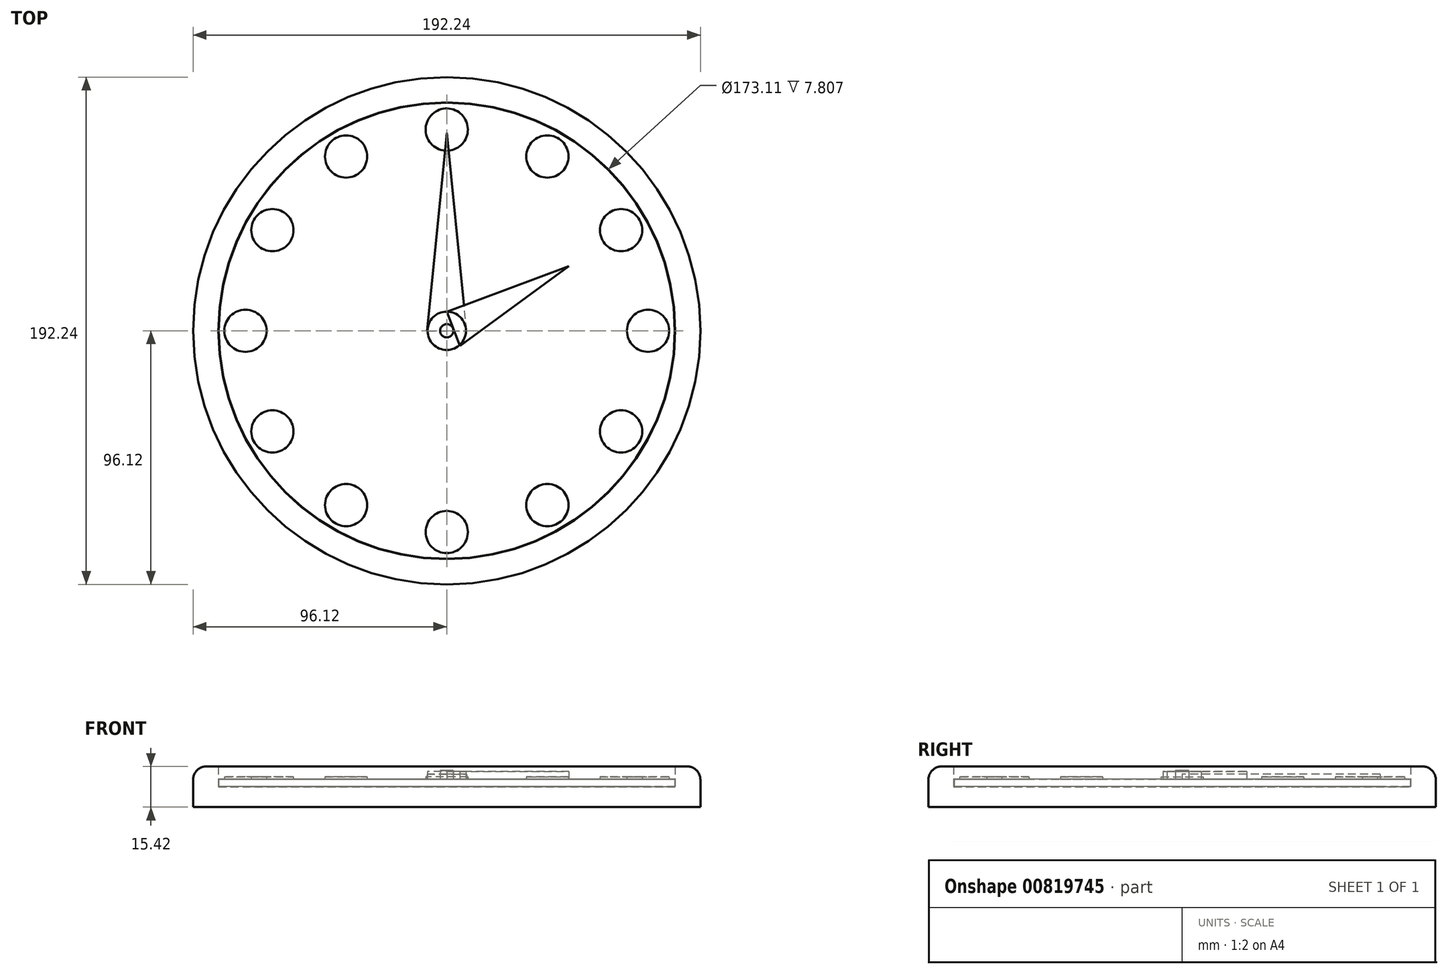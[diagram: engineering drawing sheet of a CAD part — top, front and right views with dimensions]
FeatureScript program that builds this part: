
annotation { "Feature Type Name" : "Feature", "Feature Type Description" : "" }
export const myFeature = defineFeature(function(context is Context, id is Id, definition is map)
    precondition{}
    {
        {
            var Q0;
            Q0=qCreatedBy(makeId("Front.planeOp"),FACE);
            var sketch = newSketch(context, id + "F0", { "sketchPlane" : qUnion([Q0])});
            skLineSegment(sketch, "E0", {"start": v(-96.12, 15.42) * mm, "end": v(-86.56, 15.42) * mm});
            skLineSegment(sketch, "E1", {"start": v(-86.56, 15.42) * mm, "end": v(-86.56, 7.61) * mm});
            skLineSegment(sketch, "E2", {"start": v(-86.56, 7.61) * mm, "end": v(0, 7.61) * mm});
            skLineSegment(sketch, "E3", {"start": v(0, 7.61) * mm, "end": v(0, 0) * mm});
            skLineSegment(sketch, "E4", {"start": v(0, 7.61) * mm, "end": v(0, 30.45) * mm, "construction": true});
            skLineSegment(sketch, "E5", {"start": v(-96.12, 15.42) * mm, "end": v(-96.12, 0) * mm});
            skLineSegment(sketch, "E6", {"start": v(-96.12, 0) * mm, "end": v(0, 0) * mm});
            skSolve(sketch);
        }
        {
            var Q0;
            Q0=makeQuery(id+"F0.imprint","IMPRINT",FACE,{"disambiguationData":[TD([[makeQuery(id+"F0.imprint","IMPRINT",EDGE,{"derivedFrom":sQuery(id+"F0.wireOp",EDGE,"E0")}),-1.0]])]});
            var Q1;
            Q1=sQuery(id+"F0.wireOp",EDGE,"E4");
            revolve(context, id + "F1", {"surfaceOperationType" : NewSurfaceOperationType.NEW, "entities" : qUnion([Q0]), "axis" : qUnion([Q1]), "revolveType" : RevolveType.FULL});
        }
        {
            var Q0;
            Q0=qCreatedBy(makeId("Right.planeOp"),FACE);
            var sketch = newSketch(context, id + "F2", { "sketchPlane" : qUnion([Q0])});
            skLineSegment(sketch, "E7", {"start": v(-86.42, 10.54) * mm, "end": v(0, 10.54) * mm});
            skLineSegment(sketch, "E8", {"start": v(0, 10.54) * mm, "end": v(0, 7.8) * mm});
            skLineSegment(sketch, "E9", {"start": v(0, 7.8) * mm, "end": v(-86.42, 7.8) * mm});
            skLineSegment(sketch, "E10", {"start": v(-86.42, 7.8) * mm, "end": v(-86.42, 10.54) * mm});
            skSolve(sketch);
        }
        {
            var Q0;
            Q0=makeQuery(id+"F2.imprint","IMPRINT",FACE,{"disambiguationData":[TD([[makeQuery(id+"F2.imprint","IMPRINT",EDGE,{"derivedFrom":sQuery(id+"F2.wireOp",EDGE,"E7")}),-1.0]])]});
            var Q1;
            Q1=sQuery(id+"F0.wireOp",EDGE,"E4");
            revolve(context, id + "F3", {"surfaceOperationType" : NewSurfaceOperationType.NEW, "entities" : qUnion([Q0]), "axis" : qUnion([Q1]), "revolveType" : RevolveType.FULL});
        }
        {
            var Q0;
            Q0=makeQuery(id+"F1.opRevolve","SWEPT_EDGE",EDGE,{"disambiguationData":[OSD([sQuery(id+"F0.wireOp",EDGE,"E0"),sQuery(id+"F0.wireOp",EDGE,"E5")])]});
            fillet(context, id + "F4", {"entities" : qUnion([Q0]), "radius" : 5 * mm, "tangentPropagation" : true, "allowEdgeOverflow" : false});
        }
        {
            var Q0;
            Q0=makeQuery(id+"F3.opRevolve","SWEPT_FACE",FACE,{"disambiguationData":[OSD([sQuery(id+"F2.wireOp",EDGE,"E7")])]});
            var sketch = newSketch(context, id + "F5", { "sketchPlane" : qUnion([Q0])});
            skCircle(sketch, "E11", {"center": v(0, 0) * mm, "radius": 2.5 * mm});
            skSolve(sketch);
        }
        {
            var Q0;
            Q0=makeQuery(id+"F5.imprint","IMPRINT",FACE,{"disambiguationData":[TD([[makeQuery(id+"F5.imprint","IMPRINT",EDGE,{"derivedFrom":sQuery(id+"F5.wireOp",EDGE,"E11")}),1.0]])]});
            var Q1;
            Q1=sQuery(id+"F5.wireOp",EDGE,"E11");
            extrude(context, id + "F6", {"entities" : qUnion([Q0]), "operationType" : NewBodyOperationType.ADD, "surfaceEntities" : qUnion([Q1]), "depth" : 3.3 * mm, "offsetDistance" : 25 * mm});
        }
        {
            var Q0;
            Q0=makeQuery(id+"F3.opRevolve","SWEPT_FACE",FACE,{"disambiguationData":[OSD([sQuery(id+"F2.wireOp",EDGE,"E7")])]});
            var sketch = newSketch(context, id + "F7", { "sketchPlane" : qUnion([Q0])});
            skCircle(sketch, "E12", {"center": v(0, 0) * mm, "radius": 1.55 * mm});
            skSolve(sketch);
        }
        {
            var Q0;
            Q0=sQuery(id+"F7.wireOp",EDGE,"E12");
            extrude(context, id + "F8", {"bodyType" : ToolBodyType.SURFACE, "surfaceEntities" : qUnion([Q0]), "depth" : 9.1 * mm, "offsetDistance" : 25 * mm});
        }
        {
            var Q0;
            Q0=makeQuery(id+"F3.opRevolve","SWEPT_FACE",FACE,{"disambiguationData":[OSD([sQuery(id+"F2.wireOp",EDGE,"E7")])]});
            var sketch = newSketch(context, id + "F9", { "sketchPlane" : qUnion([Q0])});
            skCircle(sketch, "E13", {"center": v(0, 76.29) * mm, "radius": 8 * mm});
            skSolve(sketch);
        }
        {
            var Q0;
            Q0=qCreatedBy(makeId("Front.planeOp"),FACE);
            var sketch = newSketch(context, id + "F10", { "sketchPlane" : qUnion([Q0])});
            skLineSegment(sketch, "E14", {"start": v(0, 0) * mm, "end": v(0, 73.97) * mm});
            skSolve(sketch);
        }
        {
            var Q0;
            Q0=makeQuery(id+"F9.imprint","IMPRINT",FACE,{"disambiguationData":[TD([[makeQuery(id+"F9.imprint","IMPRINT",EDGE,{"derivedFrom":sQuery(id+"F9.wireOp",EDGE,"E13")}),1.0]])]});
            var Q1;
            Q1=sQuery(id+"F9.wireOp",EDGE,"E13");
            extrude(context, id + "F11", {"entities" : qUnion([Q0]), "operationType" : NewBodyOperationType.ADD, "surfaceEntities" : qUnion([Q1]), "depth" : 0.9 * mm, "offsetDistance" : 25 * mm});
        }
        {
            var Q0;
            Q0=makeQuery(id+"F3.opRevolve","SWEPT_BODY",BODY,{"disambiguationData":[OSD([sQuery(id+"F2.wireOp",EDGE,"E7"),sQuery(id+"F2.wireOp",EDGE,"E8"),sQuery(id+"F2.wireOp",EDGE,"E9"),sQuery(id+"F2.wireOp",EDGE,"E10")])]});
            var Q1;
            Q1=sQuery(id+"F10.wireOp",EDGE,"E14");
            circularPattern(context, id + "F12", {"entities" : qUnion([Q0]), "axis" : qUnion([Q1]), "angle" : 360 * degree, "instanceCount" : 12, "equalSpace" : true});
        }
        {
            var Q0;
            Q0=makeQuery(id+"F12.opPattern","COPY",FACE,{"derivedFrom":makeQuery(id+"F3.opRevolve","SWEPT_FACE",FACE,{"disambiguationData":[OSD([sQuery(id+"F2.wireOp",EDGE,"E7")])]}),"instanceName":"4"});
            var sketch = newSketch(context, id + "F13", { "sketchPlane" : qUnion([Q0])});
            skCircle(sketch, "E15", {"center": v(0, 0) * mm, "radius": 7.27 * mm});
            skSolve(sketch);
        }
        {
            var Q0;
            Q0=makeQuery(id+"F13.imprint","IMPRINT",FACE,{"disambiguationData":[TD([[makeQuery(id+"F13.imprint","IMPRINT",EDGE,{"derivedFrom":sQuery(id+"F13.wireOp",EDGE,"E15")}),-1.0]])]});
            var sketch = newSketch(context, id + "F14", { "sketchPlane" : qUnion([Q0])});
            skLineSegment(sketch, "E16", {"start": v(0, 75.04) * mm, "end": v(-7.48, 0) * mm});
            skLineSegment(sketch, "E17", {"start": v(-7.48, 0) * mm, "end": v(7.53, 0) * mm});
            skLineSegment(sketch, "E18", {"start": v(7.53, 0) * mm, "end": v(0, 75.04) * mm});
            skSolve(sketch);
        }
        {
            var Q0;
            Q0 = qSketchRegion(id + "F14", true);
            extrude(context, id + "F15", {"entities" : qUnion([Q0]), "depth" : 2 * mm, "offsetDistance" : 25 * mm});
        }
        {
            var Q0;
            Q0 = qSketchRegion(id + "F13", true);
            var Q1;
            Q1=sQuery(id+"F13.wireOp",EDGE,"E15");
            extrude(context, id + "F16", {"entities" : qUnion([Q0]), "surfaceEntities" : qUnion([Q1]), "depth" : 3 * mm, "offsetDistance" : 25 * mm});
        }
        {
            var Q0;
            Q0=makeQuery(id+"F3.opRevolve","SWEPT_FACE",FACE,{"disambiguationData":[OSD([sQuery(id+"F2.wireOp",EDGE,"E7")])]});
            var sketch = newSketch(context, id + "F17", { "sketchPlane" : qUnion([Q0])});
            skLineSegment(sketch, "E19", {"start": v(0, 7.25) * mm, "end": v(46.3, 24.51) * mm});
            skLineSegment(sketch, "E20", {"start": v(46.3, 24.51) * mm, "end": v(5.03, -5.75) * mm});
            skLineSegment(sketch, "E21", {"start": v(5.03, -5.75) * mm, "end": v(0, 7.25) * mm});
            skSolve(sketch);
        }
        {
            var Q0;
            Q0 = qSketchRegion(id + "F17", true);
            extrude(context, id + "F18", {"entities" : qUnion([Q0]), "depth" : 3 * mm, "offsetDistance" : 25 * mm});
        }
    });
